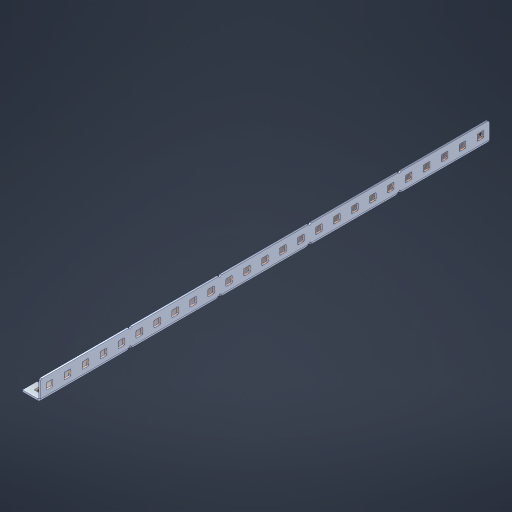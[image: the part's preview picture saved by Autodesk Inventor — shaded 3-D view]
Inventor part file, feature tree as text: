
AUTODESK INVENTOR PART (.ipt)
format: ipt  version: 2023 (Build 270158000, 158)  size: 1,063,936 bytes
history: native  units: in
note: dims shown in document units (in); Inventor stores cm internally (conversion verified against a paired STEP export)
features: other x82, extrude x73, sheet_metal_op x11, sketch x10, pattern_linear x2, mirror x1, chamfer x1
ambient origin geometry x8: Origin, YZ Plane, XZ Plane, XY Plane, X Axis, Y Axis, Z Axis, Center Point
bodies: Solid1 (feature_tree), Body (feature_tree)
feature tree (180):
  sheet_metal_op  "Flanges"
  other  "Flange Pattern Plane"
  other  "Flange Pattern Sketch"
  sheet_metal_op  "Flange Pattern"
  sheet_metal_op  "Body Pattern"
  pattern_linear  "Center Pattern"  Spacing1=0.0469in  [1 undecoded]
  other  "Arc Length"
  mirror  "Notch Mirror"
  pattern_linear  "Notch Pattern"  Spacing1=0.182in  [1 undecoded]
  chamfer  "End Chamfer"
  extrude  "Half Cut"  Depth=0.02in
  sketch  "Sketch1"  dims[d0=1.0in]
  other  "Plate1"
  sketch  "Sketch2"  dims[d1=12.5in]
  other  "Plate2"
  sheet_metal_op  "Bend1"
  sheet_metal_op  "Corner1"
  sketch  "Sketch3"  dims[d2=0.0469in]
  sketch  "Sketch7"  dims[d3=0.0469in]
  other  "Srf1"
  other  "Srf2"
  sketch  "Sketch8"  dims[d4=0.0234in]
  sketch  "Sketch9"  dims[d5=0.0938in]
  other  "Srf91"
  sheet_metal_op  "Body Pattern Sketch"
  other  "Srf92"
  sketch  "Sketch13"  dims[d6=0.0469in]
  sketch  "Sketch14"  dims[d7=0.5in d8=90.0deg d9=0.0312in]
  sketch  "Sketch15"  dims[d10=0.1875in]
  sketch  "Sketch16"  dims[d11=0.0469in d12=0.0469in d16=0.182in d17=0.02in d18=0.0469in d19=0.0in d20=0.25in d21=0.25in d38=9.8425in d40=0.5in d41=0.3937in d43=1.0in d46=0.172in d47=1.0in d48=0.0in d49=0.182in d50=0.02in d51=0.25in d52=0.25in d53=0.0469in d54=0.0in d55=0.172in d56=1.0in d57=0.0in d58=0.25in d60=9.8425in d62=0.5in d63=0.3937in d65=0.5in d85=0.1227in d86=0.1659in d88=0.04in d89=0.0469in d90=0.0in d91=0.04in d92=0.0491in d95=2.5in d96=0.04in d97=0.25in d98=45.0deg d99=0.25in d100=0.5in d101=0.0in d102=2.497in d106=0.182in d107=0.02in d108=0.5in d109=0.5in d110=0.0469in d111=0.0in d112=0.172in d113=0.5in d114=0.0in d117=0.5in d118=0.5in d119=0.5in]
  other  "Srf786"
  other  "Srf823"
  other  "Srf824"
  other  "Srf825"
  other  "Srf826"
  other  "Srf827"
  other  "Srf828"
  other  "Srf829"
  other  "Srf856"
  other  "Srf857"
  other  "Srf858"
  other  "Srf859"
  other  "Srf860"
  other  "Srf861"
  other  "Srf862"
  other  "Srf889"
  other  "Srf890"
  other  "Srf891"
  other  "Srf892"
  other  "Srf893"
  other  "Srf894"
  other  "Srf895"
  other  "Srf896"
  other  "Srf922"
  other  "Srf923"
  other  "Srf924"
  other  "Srf925"
  other  "Srf926"
  other  "Srf959"
  other  "Srf960"
  other  "Srf961"
  other  "Srf962"
  other  "Srf963"
  other  "Srf996"
  other  "Srf997"
  other  "Srf998"
  other  "Srf999"
  other  "Srf1000"
  other  "Srf1143"
  other  "Srf1144"
  other  "Srf1145"
  other  "Srf1146"
  other  "Srf1147"
  other  "Srf1148"
  other  "Srf1149"
  other  "Srf1150"
  other  "Srf1151"
  other  "Srf1152"
  other  "Srf1153"
  other  "Srf1199"
  other  "Srf1200"
  other  "Srf1201"
  other  "Srf1202"
  other  "Srf1203"
  other  "Srf1204"
  other  "Srf1205"
  other  "Srf1206"
  other  "Srf1207"
  other  "Srf1208"
  other  "Srf1209"
  other  "Srf1255"
  other  "Srf1256"
  other  "Srf1257"
  other  "Srf1258"
  other  "Srf1259"
  other  "Srf1260"
  other  "Srf1261"
  other  "Srf1262"
  other  "Srf1263"
  other  "Srf1264"
  other  "Srf1265"
  sheet_metal_op  "Flange Stamp"
  sheet_metal_op  "Flange Circle"
  sheet_metal_op  "Body Stamp"
  sheet_metal_op  "Body Circle"
  other  "Center Stamp"
  other  "Center Circle"
  sheet_metal_op  "Notch"
  extrude  "ExtrusionSrf2"  Depth=0.0469in
  extrude  "ExtrusionSrf92"  TaperAngle=0.0deg  [1 undecoded]
  extrude  "ExtrusionSrf823"  Depth=0.5in
  extrude  "ExtrusionSrf824"  Depth=0.5in
  extrude  "ExtrusionSrf825"  Depth=0.5in
  extrude  "ExtrusionSrf826"  Depth=0.5in
  extrude  "ExtrusionSrf827"  Depth=1.0in TaperAngle=0.0deg
  extrude  "ExtrusionSrf828"  Depth=0.182in
  extrude  "ExtrusionSrf829"  Depth=0.02in
  extrude  "ExtrusionSrf856"  Depth=0.5in
  extrude  "ExtrusionSrf857"  Depth=0.5in
  extrude  "ExtrusionSrf858"  Depth=0.0469in
  extrude  "ExtrusionSrf859"  TaperAngle=0.0deg  [1 undecoded]
  extrude  "ExtrusionSrf860"  Depth=0.5in
  extrude  "ExtrusionSrf861"  Depth=1.0in TaperAngle=0.0deg
  extrude  "ExtrusionSrf862"  Depth=0.5in
  extrude  "ExtrusionSrf889"  Depth=0.5in
  extrude  "ExtrusionSrf890"  Depth=0.5in
  extrude  "ExtrusionSrf891"  Depth=0.5in
  extrude  "ExtrusionSrf892"  Depth=0.5in
  extrude  "ExtrusionSrf893"  Depth=0.5in
  extrude  "ExtrusionSrf894"  Depth=0.0469in
  extrude  "ExtrusionSrf895"  TaperAngle=0.0deg  [1 undecoded]
  extrude  "ExtrusionSrf896"  Depth=0.5in
  extrude  "ExtrusionSrf922"  Depth=0.5in
  extrude  "ExtrusionSrf923"  Depth=0.5in
  extrude  "ExtrusionSrf924"  Depth=0.5in TaperAngle=45.0deg
  extrude  "ExtrusionSrf925"  Depth=0.5in
  extrude  "ExtrusionSrf926"  Depth=0.5in TaperAngle=0.0deg
  extrude  "ExtrusionSrf959"  Depth=0.5in
  extrude  "ExtrusionSrf960"  Depth=0.182in
  extrude  "ExtrusionSrf961"  Depth=0.02in
  extrude  "ExtrusionSrf962"  Depth=0.5in
  extrude  "ExtrusionSrf963"  Depth=0.5in
  extrude  "ExtrusionSrf996"  Depth=0.0469in
  extrude  "ExtrusionSrf997"  TaperAngle=0.0deg  [1 undecoded]
  extrude  "ExtrusionSrf998"  Depth=0.5in
  extrude  "ExtrusionSrf999"  Depth=0.5in TaperAngle=0.0deg
  extrude  "ExtrusionSrf1000"  Depth=0.5in
  extrude  "ExtrusionSrf1143"  Depth=0.5in
  extrude  "ExtrusionSrf1144"  Depth=0.5in
  extrude  "ExtrusionSrf1145"  [1 undecoded]
  extrude  "ExtrusionSrf1146"  [1 undecoded]
  extrude  "ExtrusionSrf1147"  [1 undecoded]
  extrude  "ExtrusionSrf1148"  [1 undecoded]
  extrude  "ExtrusionSrf1149"  [1 undecoded]
  extrude  "ExtrusionSrf1150"  [1 undecoded]
  extrude  "ExtrusionSrf1151"  [1 undecoded]
  extrude  "ExtrusionSrf1152"  [1 undecoded]
  extrude  "ExtrusionSrf1153"  [1 undecoded]
  extrude  "ExtrusionSrf1199"  [1 undecoded]
  extrude  "ExtrusionSrf1200"  [1 undecoded]
  extrude  "ExtrusionSrf1201"  [1 undecoded]
  extrude  "ExtrusionSrf1202"  [1 undecoded]
  extrude  "ExtrusionSrf1203"  [1 undecoded]
  extrude  "ExtrusionSrf1204"  [1 undecoded]
  extrude  "ExtrusionSrf1205"  [1 undecoded]
  extrude  "ExtrusionSrf1206"  [1 undecoded]
  extrude  "ExtrusionSrf1207"  [1 undecoded]
  extrude  "ExtrusionSrf1208"  [1 undecoded]
  extrude  "ExtrusionSrf1209"  [1 undecoded]
  extrude  "ExtrusionSrf1255"  [1 undecoded]
  extrude  "ExtrusionSrf1256"  [1 undecoded]
  extrude  "ExtrusionSrf1257"  [1 undecoded]
  extrude  "ExtrusionSrf1258"  [1 undecoded]
  extrude  "ExtrusionSrf1259"  [1 undecoded]
  extrude  "ExtrusionSrf1260"  [1 undecoded]
  extrude  "ExtrusionSrf1261"  [1 undecoded]
  extrude  "ExtrusionSrf1262"  [1 undecoded]
  extrude  "ExtrusionSrf1263"  [1 undecoded]
  extrude  "ExtrusionSrf1264"  [1 undecoded]
  extrude  "ExtrusionSrf1265"  [1 undecoded]
note: 37 required parameter values undecoded (feature->parameter linkage not recoverable at this tier; creation-order binding heuristic only, values carry confidence <= 0.55)
